# Revit family: 41909172
name_source: partatom
category: Plumbing Fixtures
revit_build: Autodesk Revit 2016 (Build: 20150220_1215(x64)
units: mm (PartAtom-declared; Revit-internal decimal feet)

## family parameters
Always vertical = Yes
Cut with Voids When Loaded = No
OmniClass Number = 23.45.55.00
OmniClass Title = Sanitary Faucets, Wastes
Part Type = Normal
Room Calculation Point = No
Round Connector Dimension = Use Diameter
Shared = No
Work Plane-Based = No

## types (1)
- 41909172 Cover part for shower faucet, 12 V
    2D/3D/BIM Files URL = http://static.hansa.com
    Advanced Features = Adjustable settings (with magnetic key)
    Afterflow Period = 5.0 s
    AssetType = Fixed
    BIMObjectName = 41909172
    BodyMaterial = Brass
    Brand = Hansa
    Catalog Drawing URL = http://static.hansa.com
    Category = Bathroom, shower, public & semi-public
    Class = Touchless, fixed connection, thermostatic
    CloseOffRating = 0
    Color = Chrome
    ConvergoRefNr = 0087-1809-0041-FI
    Customs Code = 84819000
    Dimension Drawing URL = http://static.hansa.com
    DurationUnit = Year
    EAN Number = 4015474277328
    EMC Directive = 2004/108/EY
    Electrical Connection = 12 VDC
    Electronic Parts = Solenoid valve, infrared sensor
    FDV Document URL = http://www.hansa.com
    FaucetMainMaterial = Brass
    Features = Touchless, fixed connection, thermostatic
    Finish = Polished
    Flow Drawing URL = http://static.hansa.com
    Flow Rate At 300kPa = 0.2 L/s
    FlowCoefficient = 0
    Group = Shower faucets
    Health Sales Arguments = Touch-free operation. Maximum comfort, maximum hygiene.
    IfcExportAs = IfcValveType
    IfcExportType = FAUCET
    Installation Type = Wall-mounted concealed
    Installation and Maintenance = http://static.hansa.com
    ManufacterURL = http://www.hansa.com
    Manufacturer = Hansa
    ManufacturerName = Hansa
    Market = BEL;CZE;DEU;ESP;FRA;INT;ITA;NLD;SVK
    Material = Brass
    Max Flow Period = 300.0 s
    Model = 41909172 Cover part for shower faucet, 12 V
    ModelReference = 41909172
    NBSDescription = Water supply fittings for baths
    NBSReference = 45-35-70/315
    Name = 41909172 Cover part for shower faucet, 12 V
    Name_en = 41909172 Cover part for shower faucet, 12 V
    NominalDepth = 42 mm  [stored 0.137795 ft]
    NominalHeight = 199 mm  [stored 0.652887 ft]
    NominalWidth = 159 mm
    Operating Voltage = 12 V
    Package Weight = 1.5 kg
    Package external Dimensions = 210 x 165 x 60
    Product Code = 41909172
    Product Datasheet = http://www.hansa.com
    Product Family = HANSAELECTRA
    Product Image URL = http://static.hansa.com
    Product URL = http://static.hansa.com
    Protection Class = IP 55
    Recognition Range = 60 cm (50 / 60 cm)
    Revision = 2
    Shape = Sculptured
    Size = 160x42x200 mm
    Spare Parts = http://static.hansa.com
    Temperature = Thermostatic temperature control, thermostatic safety stop at 38°C
    Uniclass2 = Pr_40_30_96_81
    Uniclass2015Description = Shower thermostatic water supply sets
    Uniclass2015Reference = Pr_40_20_87_81
    Usage Group = Health centers & child welfare clinics, hospitals, shower facilities (public saunas, swimming baths), schools
    Version = 2
    VersionDate = 01/01/2019
    WarrantyDescription = http://warranty.hansa.com
    WarrantyDurationUnit = Year

note: [stored X ft] marks values corroborated as IEEE doubles in the binary element streams (Revit-internal decimal feet)

## geometry (parser evidence)
native form markers: Sweep x6
no freeform markers — native parametric forms only
